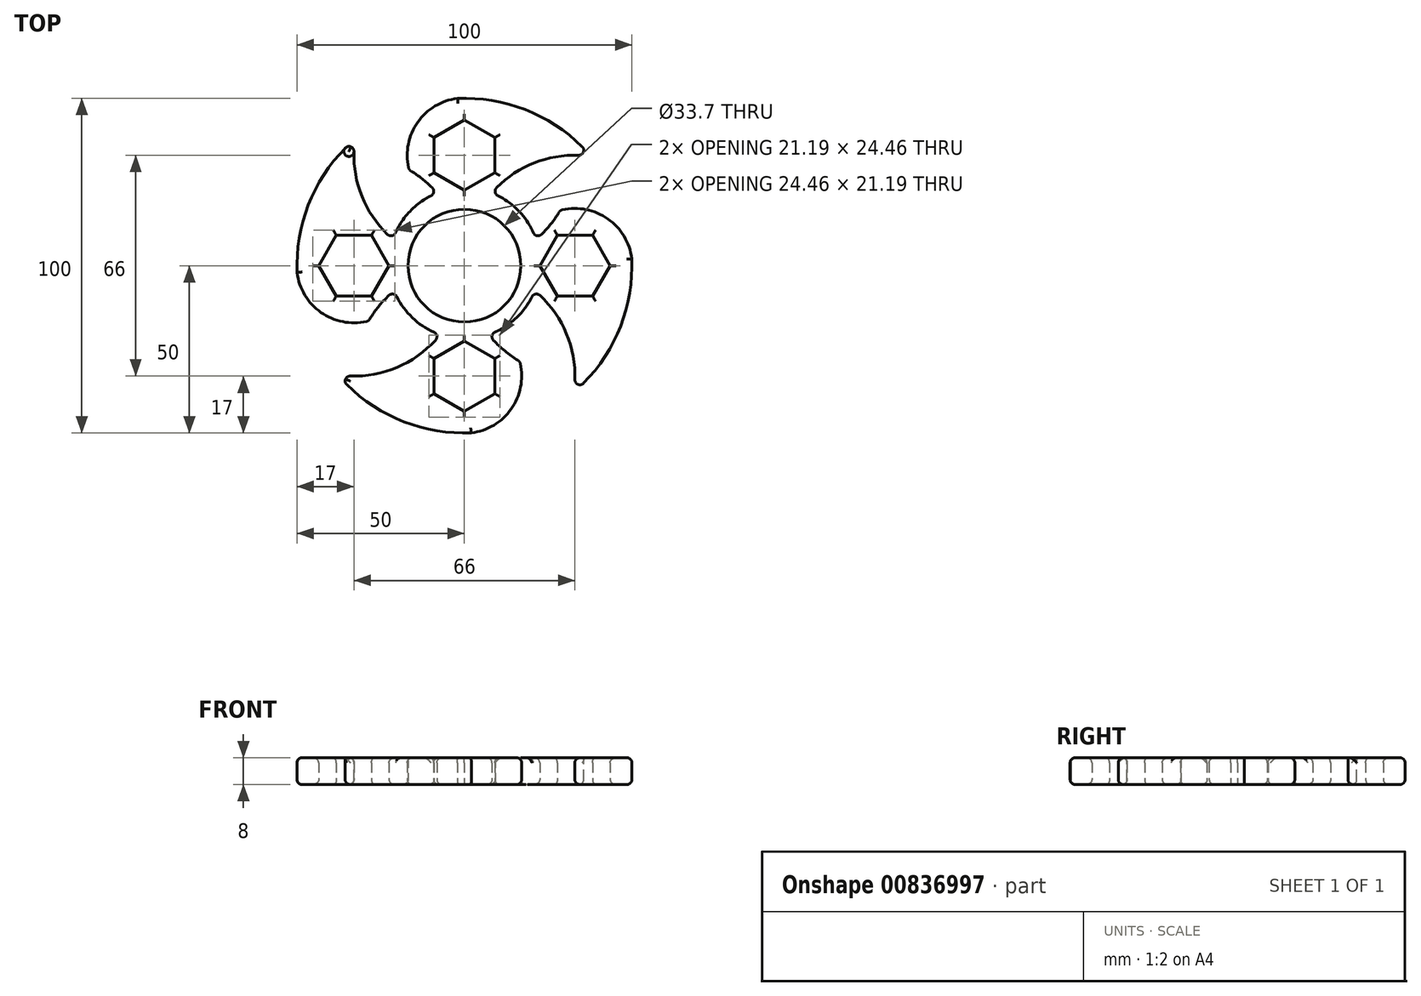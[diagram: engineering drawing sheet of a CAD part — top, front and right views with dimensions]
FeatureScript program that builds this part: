
annotation { "Feature Type Name" : "Feature", "Feature Type Description" : "" }
export const myFeature = defineFeature(function(context is Context, id is Id, definition is map)
    precondition{}
    {
        {
            var Q0;
            Q0=qCreatedBy(makeId("Top.planeOp"),FACE);
            var sketch = newSketch(context, id + "F0", { "sketchPlane" : qUnion([Q0])});
            skCircle(sketch, "E0", {"center": v(0, 0) * mm, "radius": 16.85 * mm});
            skLineSegment(sketch, "E1.0", {"start": v(-22.5, 0) * mm, "end": v(-27.75, -9.1) * mm});
            skLineSegment(sketch, "E1.1", {"start": v(-27.75, -9.1) * mm, "end": v(-38.25, -9.1) * mm});
            skLineSegment(sketch, "E1.2", {"start": v(-38.25, -9.1) * mm, "end": v(-43.5, 0) * mm});
            skLineSegment(sketch, "E1.3", {"start": v(-43.5, 0) * mm, "end": v(-38.25, 9.1) * mm});
            skLineSegment(sketch, "E1.4", {"start": v(-38.25, 9.1) * mm, "end": v(-27.75, 9.1) * mm});
            skLineSegment(sketch, "E1.5", {"start": v(-27.75, 9.1) * mm, "end": v(-22.5, 0) * mm});
            skLineSegment(sketch, "E2.0", {"start": v(0, 22.5) * mm, "end": v(-9.1, 27.75) * mm});
            skLineSegment(sketch, "E2.1", {"start": v(-9.1, 27.75) * mm, "end": v(-9.1, 38.25) * mm});
            skLineSegment(sketch, "E2.2", {"start": v(-9.1, 38.25) * mm, "end": v(0, 43.5) * mm});
            skLineSegment(sketch, "E2.3", {"start": v(0, 43.5) * mm, "end": v(9.1, 38.25) * mm});
            skLineSegment(sketch, "E2.4", {"start": v(9.1, 38.25) * mm, "end": v(9.1, 27.75) * mm});
            skLineSegment(sketch, "E2.5", {"start": v(9.1, 27.75) * mm, "end": v(0, 22.5) * mm});
            skLineSegment(sketch, "E3.0", {"start": v(22.5, 0) * mm, "end": v(27.75, 9.1) * mm});
            skLineSegment(sketch, "E3.1", {"start": v(27.75, 9.1) * mm, "end": v(38.25, 9.1) * mm});
            skLineSegment(sketch, "E3.2", {"start": v(38.25, 9.1) * mm, "end": v(43.5, 0) * mm});
            skLineSegment(sketch, "E3.3", {"start": v(43.5, 0) * mm, "end": v(38.25, -9.1) * mm});
            skLineSegment(sketch, "E3.4", {"start": v(38.25, -9.1) * mm, "end": v(27.75, -9.1) * mm});
            skLineSegment(sketch, "E3.5", {"start": v(27.75, -9.1) * mm, "end": v(22.5, 0) * mm});
            skLineSegment(sketch, "E4.0", {"start": v(0, -22.5) * mm, "end": v(9.1, -27.75) * mm});
            skLineSegment(sketch, "E4.1", {"start": v(9.1, -27.75) * mm, "end": v(9.1, -38.25) * mm});
            skLineSegment(sketch, "E4.2", {"start": v(9.1, -38.25) * mm, "end": v(0, -43.5) * mm});
            skLineSegment(sketch, "E4.3", {"start": v(0, -43.5) * mm, "end": v(-9.1, -38.25) * mm});
            skLineSegment(sketch, "E4.4", {"start": v(-9.1, -38.25) * mm, "end": v(-9.1, -27.75) * mm});
            skLineSegment(sketch, "E4.5", {"start": v(-9.1, -27.75) * mm, "end": v(0, -22.5) * mm});
            skArc(sketch, "E5", {"start": v(32.64, -37.88) * mm, "mid": v(30.8, -21.15) * mm, "end": v(20.96, -7.5) * mm});
            skArc(sketch, "E6", {"start": v(37.88, 32.64) * mm, "mid": v(21.6, 30.97) * mm, "end": v(8.13, 21.69) * mm});
            skArc(sketch, "E7", {"start": v(-32.64, 37.88) * mm, "mid": v(-45.87, 19.9) * mm, "end": v(-49.96, -2.06) * mm});
            skPoint(sketch, "E8", {"position": v(-28.58, -16.5) * mm});
            skArc(sketch, "E9.trimOffspring", {"start": v(-49.96, -2.06) * mm, "mid": v(-42.56, -14.15) * mm, "end": v(-28.58, -16.5) * mm});
            skArc(sketch, "E10.trimOffspring", {"start": v(-37.88, -32.64) * mm, "mid": v(-20.94, -30.72) * mm, "end": v(-7.22, -20.6) * mm});
            skArc(sketch, "E11.trimOffspring", {"start": v(0, -0.7) * mm, "mid": v(0, -0.7) * mm, "end": v(0, -0.7) * mm});
            skArc(sketch, "E12.trimOffspring", {"start": v(-32.64, 37.88) * mm, "mid": v(-30.89, 21.38) * mm, "end": v(-21.34, 7.82) * mm});
            skArc(sketch, "E13.trimOffspring", {"start": v(-8.12, 21.68) * mm, "mid": v(-12.03, 25.48) * mm, "end": v(-16.5, 28.58) * mm});
            skArc(sketch, "E14.trimOffspring", {"start": v(-2.06, 49.96) * mm, "mid": v(-14.15, 42.56) * mm, "end": v(-16.5, 28.58) * mm});
            skArc(sketch, "E15.trimOffspring", {"start": v(37.88, 32.64) * mm, "mid": v(19.9, 45.87) * mm, "end": v(-2.06, 49.96) * mm});
            skArc(sketch, "E16.trimOffspring", {"start": v(49.96, 2.06) * mm, "mid": v(42.56, 14.15) * mm, "end": v(28.58, 16.5) * mm});
            skArc(sketch, "E17.trimOffspring", {"start": v(-37.88, -32.64) * mm, "mid": v(-19.9, -45.87) * mm, "end": v(2.06, -49.96) * mm});
            skArc(sketch, "E18.trimOffspring", {"start": v(32.64, -37.88) * mm, "mid": v(45.87, -19.9) * mm, "end": v(49.96, 2.06) * mm});
            skArc(sketch, "E19.trimOffspring", {"start": v(2.06, -49.96) * mm, "mid": v(14.15, -42.56) * mm, "end": v(16.5, -28.58) * mm});
            skArc(sketch, "E20.trimOffspring", {"start": v(-20.94, -7.5) * mm, "mid": v(-25.17, -11.66) * mm, "end": v(-28.58, -16.5) * mm});
            skArc(sketch, "E21.trimOffspring", {"start": v(0, 0.7) * mm, "mid": v(0, 0.7) * mm, "end": v(0, 0.7) * mm});
            skArc(sketch, "E22.trimOffspring", {"start": v(7.23, -20.6) * mm, "mid": v(11.5, -25.03) * mm, "end": v(16.5, -28.58) * mm});
            skArc(sketch, "E23.trimOffspring", {"start": v(21.35, 7.83) * mm, "mid": v(25.34, 11.86) * mm, "end": v(28.58, 16.5) * mm});
            skCircle(sketch, "E24", {"center": v(0, 0.7) * mm, "radius": 22.5 * mm});
            skSolve(sketch);
        }
        {
            var Q0;
            Q0=qSketchRegion(id+"F0",true);
            extrude(context, id + "F1", {"entities" : qUnion([Q0]), "depth" : 8 * mm, "offsetDistance" : 25 * mm});
        }
        {
            var Q0;
            Q0=makeQuery(id+"F1.opExtrude","CAP_EDGE",EDGE,{"disambiguationData":[OSD([sQuery(id+"F0.wireOp",EDGE,"E4.3")])],"isStart":false});
            var Q1;
            Q1=makeQuery(id+"F1.opExtrude","CAP_EDGE",EDGE,{"disambiguationData":[OSD([sQuery(id+"F0.wireOp",EDGE,"E4.2")])],"isStart":false});
            var Q2;
            Q2=makeQuery(id+"F1.opExtrude","CAP_EDGE",EDGE,{"disambiguationData":[OSD([sQuery(id+"F0.wireOp",EDGE,"E4.4")])],"isStart":false});
            var Q3;
            Q3=makeQuery(id+"F1.opExtrude","CAP_EDGE",EDGE,{"disambiguationData":[OSD([sQuery(id+"F0.wireOp",EDGE,"E4.5")])],"isStart":false});
            var Q4;
            Q4=makeQuery(id+"F1.opExtrude","CAP_EDGE",EDGE,{"disambiguationData":[OSD([sQuery(id+"F0.wireOp",EDGE,"E4.0")])],"isStart":false});
            var Q5;
            Q5=makeQuery(id+"F1.opExtrude","CAP_EDGE",EDGE,{"disambiguationData":[OSD([sQuery(id+"F0.wireOp",EDGE,"E4.1")])],"isStart":false});
            var Q6;
            Q6=makeQuery(id+"F1.opExtrude","CAP_EDGE",EDGE,{"disambiguationData":[OSD([sQuery(id+"F0.wireOp",EDGE,"E22.trimOffspring")])],"isStart":false});
            var Q7;
            Q7=makeQuery(id+"F1.opExtrude","CAP_EDGE",EDGE,{"disambiguationData":[OSD([sQuery(id+"F0.wireOp",EDGE,"E19.trimOffspring")])],"isStart":false});
            var Q8;
            Q8=makeQuery(id+"F1.opExtrude","SWEPT_EDGE",EDGE,{"disambiguationData":[OSD([sQuery(id+"F0.wireOp",EDGE,"E19.trimOffspring"),sQuery(id+"F0.wireOp",EDGE,"E22.trimOffspring")])]});
            var Q9;
            Q9=makeQuery(id+"F1.opExtrude","CAP_EDGE",EDGE,{"disambiguationData":[OSD([sQuery(id+"F0.wireOp",EDGE,"E10.trimOffspring")])],"isStart":false});
            var Q10;
            Q10=makeQuery(id+"F1.opExtrude","CAP_EDGE",EDGE,{"disambiguationData":[OSD([sQuery(id+"F0.wireOp",EDGE,"cec13cf1-9b45-4664-9f0a-28c04969c481.trimOffspring")])],"isStart":false});
            var Q11;
            Q11=makeQuery(id+"F1.opExtrude","SWEPT_EDGE",EDGE,{"disambiguationData":[OSD([sQuery(id+"F0.wireOp",EDGE,"E22.trimOffspring"),sQuery(id+"F0.wireOp",EDGE,"cec13cf1-9b45-4664-9f0a-28c04969c481.trimOffspring")])]});
            var Q12;
            Q12=makeQuery(id+"F1.opExtrude","CAP_EDGE",EDGE,{"disambiguationData":[OSD([sQuery(id+"F0.wireOp",EDGE,"E5")])],"isStart":false});
            var Q13;
            Q13=makeQuery(id+"F1.opExtrude","CAP_EDGE",EDGE,{"disambiguationData":[OSD([sQuery(id+"F0.wireOp",EDGE,"E23.trimOffspring")])],"isStart":false});
            var Q14;
            Q14=makeQuery(id+"F1.opExtrude","SWEPT_EDGE",EDGE,{"disambiguationData":[OSD([sQuery(id+"F0.wireOp",EDGE,"E6"),sQuery(id+"F0.wireOp",EDGE,"64fbe1ca-0ee3-437b-a6b5-f8acca399637.trimOffspring")])]});
            var Q15;
            Q15=makeQuery(id+"F1.opExtrude","CAP_EDGE",EDGE,{"disambiguationData":[OSD([sQuery(id+"F0.wireOp",EDGE,"64fbe1ca-0ee3-437b-a6b5-f8acca399637.trimOffspring")])],"isStart":false});
            var Q16;
            Q16=makeQuery(id+"F1.opExtrude","CAP_EDGE",EDGE,{"disambiguationData":[OSD([sQuery(id+"F0.wireOp",EDGE,"E15.trimOffspring")])],"isStart":false});
            var Q17;
            Q17=makeQuery(id+"F1.opExtrude","CAP_EDGE",EDGE,{"disambiguationData":[OSD([sQuery(id+"F0.wireOp",EDGE,"E13.trimOffspring")])],"isStart":false});
            var Q18;
            Q18=makeQuery(id+"F1.opExtrude","CAP_EDGE",EDGE,{"disambiguationData":[OSD([sQuery(id+"F0.wireOp",EDGE,"E14.trimOffspring")])],"isStart":false});
            var Q19;
            Q19=makeQuery(id+"F1.opExtrude","CAP_EDGE",EDGE,{"disambiguationData":[OSD([sQuery(id+"F0.wireOp",EDGE,"E12.trimOffspring")])],"isStart":false});
            var Q20;
            Q20=makeQuery(id+"F1.opExtrude","CAP_EDGE",EDGE,{"disambiguationData":[OSD([sQuery(id+"F0.wireOp",EDGE,"E12.trimOffspring")])],"isStart":true});
            var Q21;
            Q21=makeQuery(id+"F1.opExtrude","SWEPT_EDGE",EDGE,{"disambiguationData":[OSD([sQuery(id+"F0.wireOp",EDGE,"E9.trimOffspring"),sQuery(id+"F0.wireOp",EDGE,"E20.trimOffspring")])]});
            var Q22;
            Q22=makeQuery(id+"F1.opExtrude","CAP_EDGE",EDGE,{"disambiguationData":[OSD([sQuery(id+"F0.wireOp",EDGE,"E20.trimOffspring")])],"isStart":true});
            var Q23;
            Q23=makeQuery(id+"F1.opExtrude","CAP_EDGE",EDGE,{"disambiguationData":[OSD([sQuery(id+"F0.wireOp",EDGE,"E20.trimOffspring")])],"isStart":false});
            var Q24;
            Q24=makeQuery(id+"F1.opExtrude","CAP_EDGE",EDGE,{"disambiguationData":[OSD([sQuery(id+"F0.wireOp",EDGE,"532945e2-2742-4c00-85bd-60de8ac5743c.trimOffspring")])],"isStart":false});
            var Q25;
            Q25=makeQuery(id+"F1.opExtrude","CAP_EDGE",EDGE,{"disambiguationData":[OSD([sQuery(id+"F0.wireOp",EDGE,"uSXMq6lJ-faUj-PYge-tHJH-Hq22nSB10Fme")])],"isStart":false});
            var Q26;
            Q26=makeQuery(id+"F1.opExtrude","CAP_EDGE",EDGE,{"disambiguationData":[OSD([sQuery(id+"F0.wireOp",EDGE,"E1.0")])],"isStart":false});
            var Q27;
            Q27=makeQuery(id+"F1.opExtrude","CAP_EDGE",EDGE,{"disambiguationData":[OSD([sQuery(id+"F0.wireOp",EDGE,"E1.1")])],"isStart":false});
            var Q28;
            Q28=makeQuery(id+"F1.opExtrude","CAP_EDGE",EDGE,{"disambiguationData":[OSD([sQuery(id+"F0.wireOp",EDGE,"E1.2")])],"isStart":false});
            var Q29;
            Q29=makeQuery(id+"F1.opExtrude","CAP_EDGE",EDGE,{"disambiguationData":[OSD([sQuery(id+"F0.wireOp",EDGE,"E1.3")])],"isStart":false});
            var Q30;
            Q30=makeQuery(id+"F1.opExtrude","CAP_EDGE",EDGE,{"disambiguationData":[OSD([sQuery(id+"F0.wireOp",EDGE,"E1.4")])],"isStart":false});
            var Q31;
            Q31=makeQuery(id+"F1.opExtrude","CAP_EDGE",EDGE,{"disambiguationData":[OSD([sQuery(id+"F0.wireOp",EDGE,"E1.5")])],"isStart":false});
            var Q32;
            Q32=makeQuery(id+"F1.opExtrude","CAP_EDGE",EDGE,{"disambiguationData":[OSD([sQuery(id+"F0.wireOp",EDGE,"E18.trimOffspring")])],"isStart":false});
            var Q33;
            Q33=makeQuery(id+"F1.opExtrude","CAP_EDGE",EDGE,{"disambiguationData":[OSD([sQuery(id+"F0.wireOp",EDGE,"E16.trimOffspring")])],"isStart":false});
            var Q34;
            Q34=makeQuery(id+"F1.opExtrude","CAP_EDGE",EDGE,{"disambiguationData":[OSD([sQuery(id+"F0.wireOp",EDGE,"E3.4")])],"isStart":false});
            var Q35;
            Q35=makeQuery(id+"F1.opExtrude","CAP_EDGE",EDGE,{"disambiguationData":[OSD([sQuery(id+"F0.wireOp",EDGE,"E3.5")])],"isStart":false});
            var Q36;
            Q36=makeQuery(id+"F1.opExtrude","CAP_EDGE",EDGE,{"disambiguationData":[OSD([sQuery(id+"F0.wireOp",EDGE,"E3.0")])],"isStart":false});
            var Q37;
            Q37=makeQuery(id+"F1.opExtrude","CAP_EDGE",EDGE,{"disambiguationData":[OSD([sQuery(id+"F0.wireOp",EDGE,"E3.1")])],"isStart":false});
            var Q38;
            Q38=makeQuery(id+"F1.opExtrude","CAP_EDGE",EDGE,{"disambiguationData":[OSD([sQuery(id+"F0.wireOp",EDGE,"E3.2")])],"isStart":false});
            var Q39;
            Q39=makeQuery(id+"F1.opExtrude","CAP_EDGE",EDGE,{"disambiguationData":[OSD([sQuery(id+"F0.wireOp",EDGE,"E3.3")])],"isStart":false});
            var Q40;
            Q40=makeQuery(id+"F1.opExtrude","CAP_EDGE",EDGE,{"disambiguationData":[OSD([sQuery(id+"F0.wireOp",EDGE,"E2.2")])],"isStart":false});
            var Q41;
            Q41=makeQuery(id+"F1.opExtrude","CAP_EDGE",EDGE,{"disambiguationData":[OSD([sQuery(id+"F0.wireOp",EDGE,"E2.1")])],"isStart":false});
            var Q42;
            Q42=makeQuery(id+"F1.opExtrude","CAP_EDGE",EDGE,{"disambiguationData":[OSD([sQuery(id+"F0.wireOp",EDGE,"E2.0")])],"isStart":false});
            var Q43;
            Q43=makeQuery(id+"F1.opExtrude","CAP_EDGE",EDGE,{"disambiguationData":[OSD([sQuery(id+"F0.wireOp",EDGE,"E2.5")])],"isStart":false});
            var Q44;
            Q44=makeQuery(id+"F1.opExtrude","CAP_EDGE",EDGE,{"disambiguationData":[OSD([sQuery(id+"F0.wireOp",EDGE,"E2.4")])],"isStart":false});
            var Q45;
            Q45=makeQuery(id+"F1.opExtrude","CAP_EDGE",EDGE,{"disambiguationData":[OSD([sQuery(id+"F0.wireOp",EDGE,"E2.3")])],"isStart":false});
            var Q46;
            Q46=makeQuery(id+"F1.opExtrude","CAP_EDGE",EDGE,{"disambiguationData":[OSD([sQuery(id+"F0.wireOp",EDGE,"E13.trimOffspring")])],"isStart":true});
            var Q47;
            Q47=makeQuery(id+"F1.opExtrude","CAP_EDGE",EDGE,{"disambiguationData":[OSD([sQuery(id+"F0.wireOp",EDGE,"532945e2-2742-4c00-85bd-60de8ac5743c.trimOffspring")])],"isStart":true});
            var Q48;
            Q48=makeQuery(id+"F1.opExtrude","CAP_EDGE",EDGE,{"disambiguationData":[OSD([sQuery(id+"F0.wireOp",EDGE,"E6")])],"isStart":true});
            var Q49;
            Q49=makeQuery(id+"F1.opExtrude","CAP_EDGE",EDGE,{"disambiguationData":[OSD([sQuery(id+"F0.wireOp",EDGE,"E15.trimOffspring")])],"isStart":true});
            var Q50;
            Q50=makeQuery(id+"F1.opExtrude","CAP_EDGE",EDGE,{"disambiguationData":[OSD([sQuery(id+"F0.wireOp",EDGE,"E14.trimOffspring")])],"isStart":true});
            var Q51;
            Q51=makeQuery(id+"F1.opExtrude","CAP_EDGE",EDGE,{"disambiguationData":[OSD([sQuery(id+"F0.wireOp",EDGE,"E7")])],"isStart":true});
            var Q52;
            Q52=makeQuery(id+"F1.opExtrude","CAP_EDGE",EDGE,{"disambiguationData":[OSD([sQuery(id+"F0.wireOp",EDGE,"E9.trimOffspring")])],"isStart":true});
            var Q53;
            Q53=makeQuery(id+"F1.opExtrude","CAP_EDGE",EDGE,{"disambiguationData":[OSD([sQuery(id+"F0.wireOp",EDGE,"E1.3")])],"isStart":true});
            var Q54;
            Q54=makeQuery(id+"F1.opExtrude","CAP_EDGE",EDGE,{"disambiguationData":[OSD([sQuery(id+"F0.wireOp",EDGE,"E1.4")])],"isStart":true});
            var Q55;
            Q55=makeQuery(id+"F1.opExtrude","CAP_EDGE",EDGE,{"disambiguationData":[OSD([sQuery(id+"F0.wireOp",EDGE,"E1.5")])],"isStart":true});
            var Q56;
            Q56=makeQuery(id+"F1.opExtrude","CAP_EDGE",EDGE,{"disambiguationData":[OSD([sQuery(id+"F0.wireOp",EDGE,"E1.0")])],"isStart":true});
            var Q57;
            Q57=makeQuery(id+"F1.opExtrude","CAP_EDGE",EDGE,{"disambiguationData":[OSD([sQuery(id+"F0.wireOp",EDGE,"E1.1")])],"isStart":true});
            var Q58;
            Q58=makeQuery(id+"F1.opExtrude","CAP_EDGE",EDGE,{"disambiguationData":[OSD([sQuery(id+"F0.wireOp",EDGE,"E1.2")])],"isStart":true});
            var Q59;
            Q59=makeQuery(id+"F1.opExtrude","CAP_EDGE",EDGE,{"disambiguationData":[OSD([sQuery(id+"F0.wireOp",EDGE,"uSXMq6lJ-faUj-PYge-tHJH-Hq22nSB10Fme")])],"isStart":true});
            var Q60;
            Q60=makeQuery(id+"F1.opExtrude","CAP_EDGE",EDGE,{"disambiguationData":[OSD([sQuery(id+"F0.wireOp",EDGE,"cec13cf1-9b45-4664-9f0a-28c04969c481.trimOffspring")])],"isStart":true});
            var Q61;
            Q61=makeQuery(id+"F1.opExtrude","CAP_EDGE",EDGE,{"disambiguationData":[OSD([sQuery(id+"F0.wireOp",EDGE,"E5")])],"isStart":true});
            var Q62;
            Q62=makeQuery(id+"F1.opExtrude","CAP_EDGE",EDGE,{"disambiguationData":[OSD([sQuery(id+"F0.wireOp",EDGE,"E23.trimOffspring")])],"isStart":true});
            var Q63;
            Q63=makeQuery(id+"F1.opExtrude","CAP_EDGE",EDGE,{"disambiguationData":[OSD([sQuery(id+"F0.wireOp",EDGE,"E16.trimOffspring")])],"isStart":true});
            var Q64;
            Q64=makeQuery(id+"F1.opExtrude","CAP_EDGE",EDGE,{"disambiguationData":[OSD([sQuery(id+"F0.wireOp",EDGE,"E17.trimOffspring")])],"isStart":true});
            var Q65;
            Q65=makeQuery(id+"F1.opExtrude","CAP_EDGE",EDGE,{"disambiguationData":[OSD([sQuery(id+"F0.wireOp",EDGE,"E19.trimOffspring")])],"isStart":true});
            var Q66;
            Q66=makeQuery(id+"F1.opExtrude","CAP_EDGE",EDGE,{"disambiguationData":[OSD([sQuery(id+"F0.wireOp",EDGE,"E10.trimOffspring")])],"isStart":true});
            var Q67;
            Q67=makeQuery(id+"F1.opExtrude","SWEPT_EDGE",EDGE,{"disambiguationData":[OSD([sQuery(id+"F0.wireOp",EDGE,"E5"),sQuery(id+"F0.wireOp",EDGE,"cec13cf1-9b45-4664-9f0a-28c04969c481.trimOffspring")])]});
            var Q68;
            Q68=makeQuery(id+"F1.opExtrude","SWEPT_EDGE",EDGE,{"disambiguationData":[OSD([sQuery(id+"F0.wireOp",EDGE,"E12.trimOffspring"),sQuery(id+"F0.wireOp",EDGE,"532945e2-2742-4c00-85bd-60de8ac5743c.trimOffspring")])]});
            var Q69;
            Q69=makeQuery(id+"F1.opExtrude","SWEPT_EDGE",EDGE,{"disambiguationData":[OSD([sQuery(id+"F0.wireOp",EDGE,"64fbe1ca-0ee3-437b-a6b5-f8acca399637.trimOffspring"),sQuery(id+"F0.wireOp",EDGE,"E23.trimOffspring")])]});
            var Q70;
            Q70=makeQuery(id+"F1.opExtrude","SWEPT_EDGE",EDGE,{"disambiguationData":[OSD([sQuery(id+"F0.wireOp",EDGE,"E13.trimOffspring"),sQuery(id+"F0.wireOp",EDGE,"532945e2-2742-4c00-85bd-60de8ac5743c.trimOffspring")])]});
            var Q71;
            {var subQ0=sQuery(id+"F0.wireOp",EDGE,"E24");Q71=makeQuery(id+"F1.opExtrude","CAP_EDGE",EDGE,{"disambiguationData":[OSD([subQ0]),TDD([makeQuery(id+"F0.imprint","IMPRINT",EDGE,{"disambiguationData":[TD([[makeQuery(id+"F0.imprint","INTERSECT",VERTEX,{"derivedFrom":[sQuery(id+"F0.wireOp",EDGE,"E10.trimOffspring"),subQ0]}),1.0]])],"derivedFrom":subQ0})])],"isStart":false});}
            var Q72;
            Q72=makeQuery(id+"F1.opExtrude","CAP_EDGE",EDGE,{"disambiguationData":[OSD([sQuery(id+"F0.wireOp",EDGE,"E9.trimOffspring")])],"isStart":false});
            var Q73;
            Q73=makeQuery(id+"F1.opExtrude","CAP_EDGE",EDGE,{"disambiguationData":[OSD([sQuery(id+"F0.wireOp",EDGE,"E2.4")])],"isStart":true});
            var Q74;
            Q74=makeQuery(id+"F1.opExtrude","CAP_EDGE",EDGE,{"disambiguationData":[OSD([sQuery(id+"F0.wireOp",EDGE,"E2.3")])],"isStart":true});
            var Q75;
            Q75=makeQuery(id+"F1.opExtrude","CAP_EDGE",EDGE,{"disambiguationData":[OSD([sQuery(id+"F0.wireOp",EDGE,"E2.2")])],"isStart":true});
            var Q76;
            Q76=makeQuery(id+"F1.opExtrude","CAP_EDGE",EDGE,{"disambiguationData":[OSD([sQuery(id+"F0.wireOp",EDGE,"E2.1")])],"isStart":true});
            var Q77;
            Q77=makeQuery(id+"F1.opExtrude","CAP_EDGE",EDGE,{"disambiguationData":[OSD([sQuery(id+"F0.wireOp",EDGE,"E2.0")])],"isStart":true});
            var Q78;
            Q78=makeQuery(id+"F1.opExtrude","CAP_EDGE",EDGE,{"disambiguationData":[OSD([sQuery(id+"F0.wireOp",EDGE,"E2.5")])],"isStart":true});
            var Q79;
            Q79=makeQuery(id+"F1.opExtrude","CAP_EDGE",EDGE,{"disambiguationData":[OSD([sQuery(id+"F0.wireOp",EDGE,"E3.0")])],"isStart":true});
            var Q80;
            Q80=makeQuery(id+"F1.opExtrude","CAP_EDGE",EDGE,{"disambiguationData":[OSD([sQuery(id+"F0.wireOp",EDGE,"E3.3")])],"isStart":true});
            var Q81;
            Q81=makeQuery(id+"F1.opExtrude","CAP_FACE",FACE,{"disambiguationData":[OSD([sQuery(id+"F0.wireOp",EDGE,"E0"),sQuery(id+"F0.wireOp",EDGE,"E1.0"),sQuery(id+"F0.wireOp",EDGE,"E1.1"),sQuery(id+"F0.wireOp",EDGE,"E1.2"),sQuery(id+"F0.wireOp",EDGE,"E1.3"),sQuery(id+"F0.wireOp",EDGE,"E1.4"),sQuery(id+"F0.wireOp",EDGE,"E1.5"),sQuery(id+"F0.wireOp",EDGE,"E2.0"),sQuery(id+"F0.wireOp",EDGE,"E2.1"),sQuery(id+"F0.wireOp",EDGE,"E2.2"),sQuery(id+"F0.wireOp",EDGE,"E2.3"),sQuery(id+"F0.wireOp",EDGE,"E2.4"),sQuery(id+"F0.wireOp",EDGE,"E2.5"),sQuery(id+"F0.wireOp",EDGE,"E3.0"),sQuery(id+"F0.wireOp",EDGE,"E3.1"),sQuery(id+"F0.wireOp",EDGE,"E3.2"),sQuery(id+"F0.wireOp",EDGE,"E3.3"),sQuery(id+"F0.wireOp",EDGE,"E3.4"),sQuery(id+"F0.wireOp",EDGE,"E3.5"),sQuery(id+"F0.wireOp",EDGE,"E4.0"),sQuery(id+"F0.wireOp",EDGE,"E4.1"),sQuery(id+"F0.wireOp",EDGE,"E4.2"),sQuery(id+"F0.wireOp",EDGE,"E4.3"),sQuery(id+"F0.wireOp",EDGE,"E4.4"),sQuery(id+"F0.wireOp",EDGE,"E4.5"),sQuery(id+"F0.wireOp",EDGE,"E5"),sQuery(id+"F0.wireOp",EDGE,"E6"),sQuery(id+"F0.wireOp",EDGE,"E7"),sQuery(id+"F0.wireOp",EDGE,"E9.trimOffspring"),sQuery(id+"F0.wireOp",EDGE,"E10.trimOffspring"),sQuery(id+"F0.wireOp",EDGE,"E12.trimOffspring"),sQuery(id+"F0.wireOp",EDGE,"E13.trimOffspring"),sQuery(id+"F0.wireOp",EDGE,"E14.trimOffspring"),sQuery(id+"F0.wireOp",EDGE,"E15.trimOffspring"),sQuery(id+"F0.wireOp",EDGE,"E16.trimOffspring"),sQuery(id+"F0.wireOp",EDGE,"E17.trimOffspring"),sQuery(id+"F0.wireOp",EDGE,"E18.trimOffspring"),sQuery(id+"F0.wireOp",EDGE,"E19.trimOffspring"),sQuery(id+"F0.wireOp",EDGE,"E20.trimOffspring"),sQuery(id+"F0.wireOp",EDGE,"E22.trimOffspring"),sQuery(id+"F0.wireOp",EDGE,"E23.trimOffspring"),sQuery(id+"F0.wireOp",EDGE,"E24")])],"isStart":true});
            var Q82;
            Q82=makeQuery(id+"F1.opExtrude","CAP_EDGE",EDGE,{"disambiguationData":[OSD([sQuery(id+"F0.wireOp",EDGE,"E3.5")])],"isStart":true});
            var Q83;
            Q83=makeQuery(id+"F1.opExtrude","SWEPT_EDGE",EDGE,{"disambiguationData":[OSD([sQuery(id+"F0.wireOp",EDGE,"E10.trimOffspring"),sQuery(id+"F0.wireOp",EDGE,"E17.trimOffspring")])]});
            var Q84;
            Q84=makeQuery(id+"F1.opExtrude","SWEPT_EDGE",EDGE,{"disambiguationData":[OSD([sQuery(id+"F0.wireOp",EDGE,"E10.trimOffspring"),sQuery(id+"F0.wireOp",EDGE,"E24")])]});
            var Q85;
            Q85=makeQuery(id+"F1.opExtrude","SWEPT_EDGE",EDGE,{"disambiguationData":[OSD([sQuery(id+"F0.wireOp",EDGE,"E20.trimOffspring"),sQuery(id+"F0.wireOp",EDGE,"E24")])]});
            fillet(context, id + "F2", {"entities" : qUnion([Q0, Q1, Q2, Q3, Q4, Q5, Q6, Q7, Q8, Q9, Q10, Q11, Q12, Q13, Q14, Q15, Q16, Q17, Q18, Q19, Q20, Q21, Q22, Q23, Q24, Q25, Q26, Q27, Q28, Q29, Q30, Q31, Q32, Q33, Q34, Q35, Q36, Q37, Q38, Q39, Q40, Q41, Q42, Q43, Q44, Q45, Q46, Q47, Q48, Q49, Q50, Q51, Q52, Q53, Q54, Q55, Q56, Q57, Q58, Q59, Q60, Q61, Q62, Q63, Q64, Q65, Q66, Q67, Q68, Q69, Q70, Q71, Q72, Q73, Q74, Q75, Q76, Q77, Q78, Q79, Q80, Q81, Q82, Q83, Q84, Q85]), "radius" : 1.5 * mm, "tangentPropagation" : true, "allowEdgeOverflow" : false});
        }
    });
